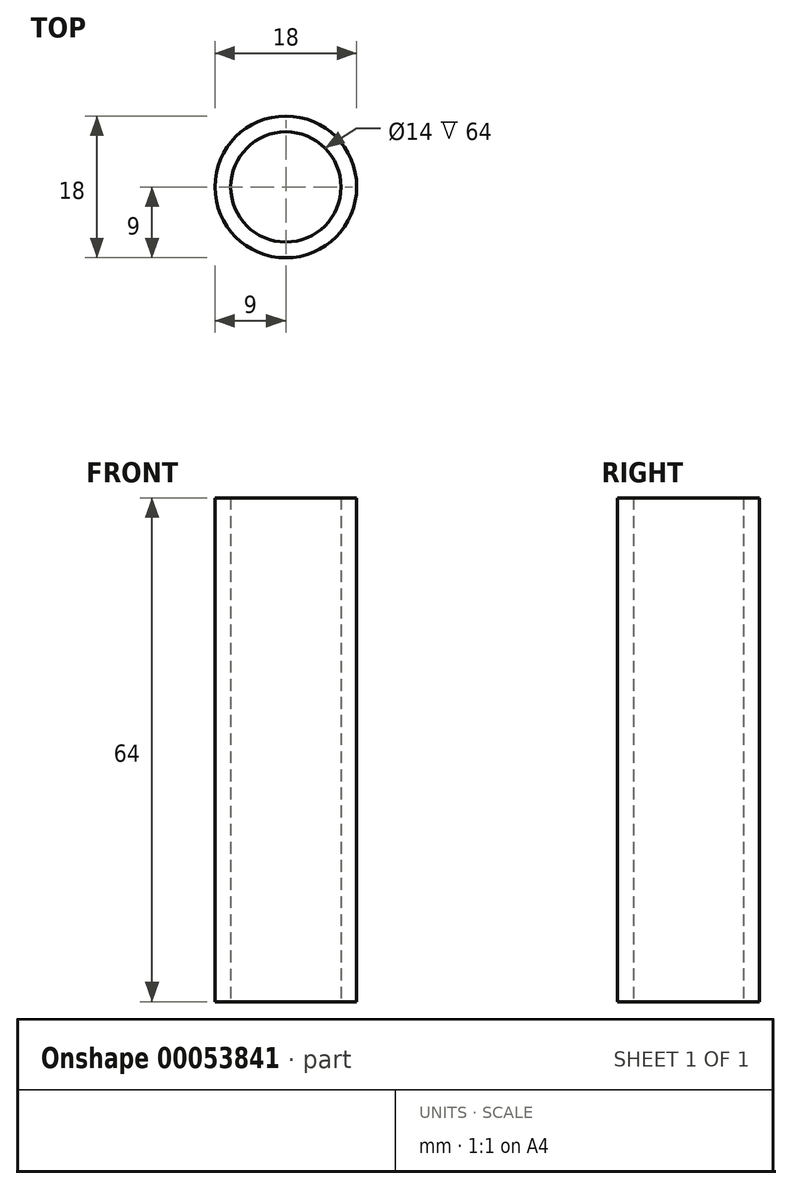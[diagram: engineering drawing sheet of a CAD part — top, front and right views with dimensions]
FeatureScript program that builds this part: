
annotation { "Feature Type Name" : "Feature", "Feature Type Description" : "" }
export const myFeature = defineFeature(function(context is Context, id is Id, definition is map)
    precondition{}
    {
        {
            var Q0;
            Q0=qCreatedBy(makeId("Front.planeOp"),FACE);
            var sketch = newSketch(context, id + "F0", { "sketchPlane" : qUnion([Q0])});
            skLineSegment(sketch, "E0.rect.bottom", {"start": v(9, 32) * mm, "end": v(-9, 32) * mm});
            skLineSegment(sketch, "E0.rect.top", {"start": v(9, -32) * mm, "end": v(-9, -32) * mm});
            skLineSegment(sketch, "E0.rect.left", {"start": v(9, 32) * mm, "end": v(9, -32) * mm});
            skLineSegment(sketch, "E0.rect.right", {"start": v(-9, 32) * mm, "end": v(-9, -32) * mm});
            skPoint(sketch, "E0.rect.middle", {"position": v(0, 0) * mm});
            skLineSegment(sketch, "E1", {"start": v(-7, 32) * mm, "end": v(-7, -32) * mm});
            skLineSegment(sketch, "E2.MirrorCS", {"start": v(7, 32) * mm, "end": v(7, -32) * mm});
            skLineSegment(sketch, "E3", {"start": v(0, -39.74) * mm, "end": v(0, 39.74) * mm});
            skPoint(sketch, "E3.endSnap0", {"position": v(0, 32) * mm});
            skSolve(sketch);
        }
        {
            var Q0;
            {var subQ0=sQuery(id+"F0.wireOp",EDGE,"E0.rect.right");Q0=makeQuery(id+"F0.imprint","IMPRINT",FACE,{"disambiguationData":[TD([[makeQuery(id+"F0.imprint","IMPRINT",EDGE,{"derivedFrom":subQ0}),1.0]])]});}
            var Q1;
            Q1=sQuery(id+"F0.wireOp",EDGE,"E3");
            revolve(context, id + "F1", {"entities" : qUnion([Q0]), "axis" : qUnion([Q1]), "revolveType" : RevolveType.FULL});
        }
    });
